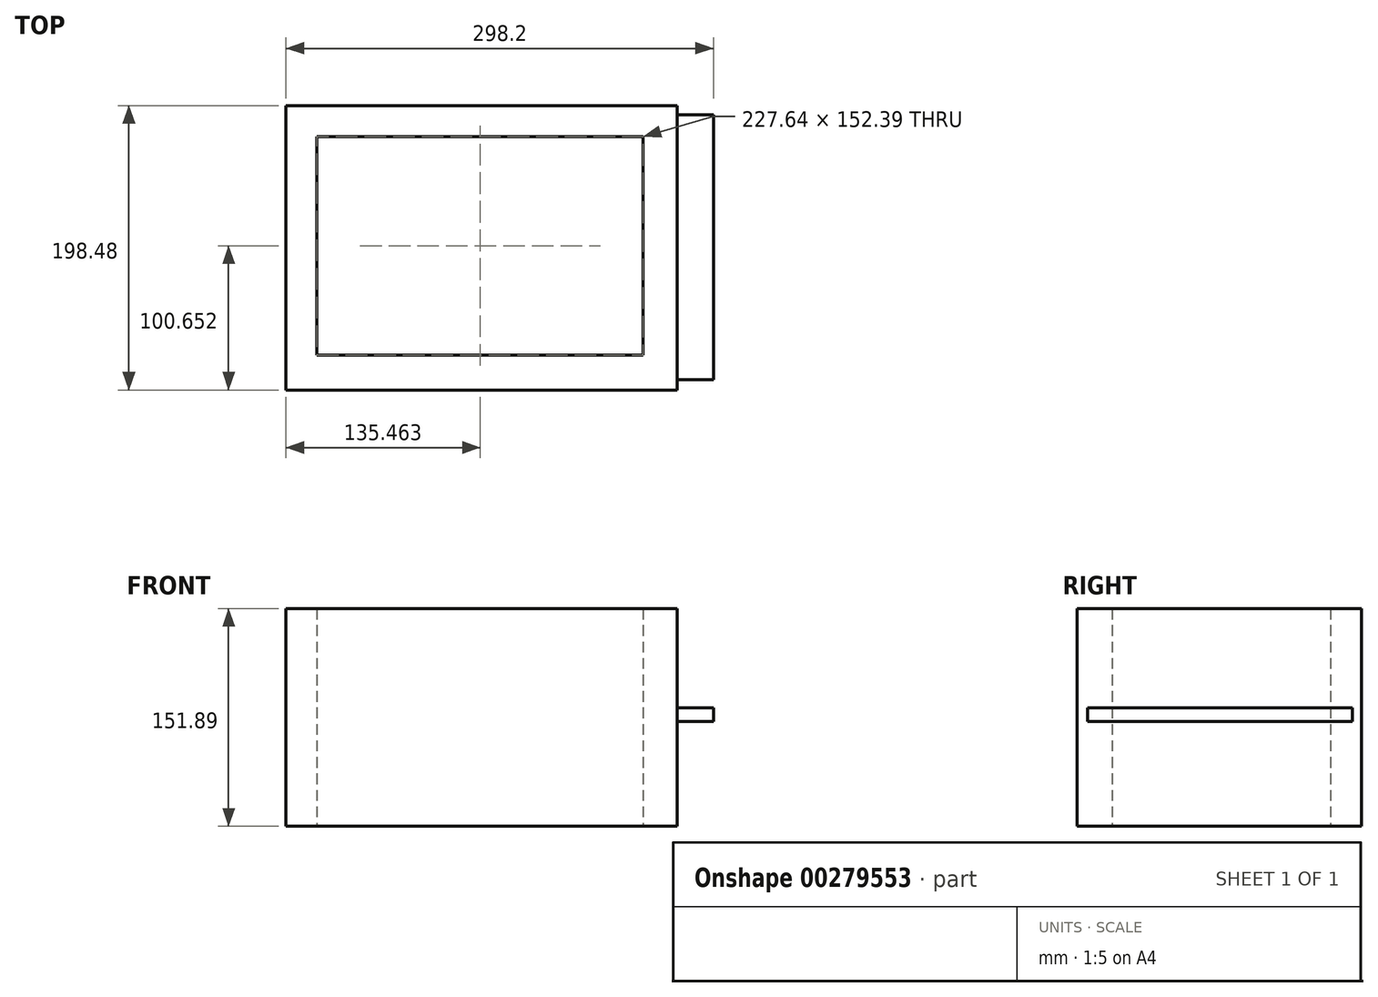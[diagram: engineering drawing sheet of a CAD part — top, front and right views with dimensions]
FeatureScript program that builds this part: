
annotation { "Feature Type Name" : "Feature", "Feature Type Description" : "" }
export const myFeature = defineFeature(function(context is Context, id is Id, definition is map)
    precondition{}
    {
        {
            var Q0;
            Q0=qCreatedBy(makeId("Top.planeOp"),FACE);
            var sketch = newSketch(context, id + "F0", { "sketchPlane" : qUnion([Q0])});
            skLineSegment(sketch, "E0.bottom", {"start": v(-52.57, 51.47) * mm, "end": v(220.23, 51.47) * mm});
            skLineSegment(sketch, "E0.top", {"start": v(-52.57, -147.01) * mm, "end": v(220.23, -147.01) * mm});
            skLineSegment(sketch, "E0.left", {"start": v(-52.57, 51.47) * mm, "end": v(-52.57, -147.01) * mm});
            skLineSegment(sketch, "E0.right", {"start": v(220.23, 51.47) * mm, "end": v(220.23, -147.01) * mm});
            skLineSegment(sketch, "E1.bottom", {"start": v(196.71, 29.84) * mm, "end": v(-30.93, 29.84) * mm});
            skLineSegment(sketch, "E1.top", {"start": v(196.71, -122.55) * mm, "end": v(-30.93, -122.55) * mm});
            skLineSegment(sketch, "E1.left", {"start": v(196.71, 29.84) * mm, "end": v(196.71, -122.55) * mm});
            skLineSegment(sketch, "E1.right", {"start": v(-30.93, 29.84) * mm, "end": v(-30.93, -122.55) * mm});
            skSolve(sketch);
        }
        {
            var Q0;
            Q0=makeQuery(id+"F0.imprint","IMPRINT",FACE,{"disambiguationData":[TD([[makeQuery(id+"F0.imprint","IMPRINT",EDGE,{"derivedFrom":sQuery(id+"F0.wireOp",EDGE,"E0.bottom")}),-1.0]])]});
            extrude(context, id + "F1", {"entities" : qUnion([Q0]), "depth" : 151.9 * mm});
        }
        {
            var Q0;
            Q0=makeQuery(id+"F1.opExtrude","SWEPT_FACE",FACE,{"disambiguationData":[OSD([sQuery(id+"F0.wireOp",EDGE,"E0.right")])]});
            var sketch = newSketch(context, id + "F2", { "sketchPlane" : qUnion([Q0])});
            skLineSegment(sketch, "E2.bottom", {"start": v(-139.82, 82.57) * mm, "end": v(44.94, 82.57) * mm});
            skLineSegment(sketch, "E2.top", {"start": v(-139.82, 73.3) * mm, "end": v(44.94, 73.3) * mm});
            skLineSegment(sketch, "E2.left", {"start": v(-139.82, 82.57) * mm, "end": v(-139.82, 73.3) * mm});
            skLineSegment(sketch, "E2.right", {"start": v(44.94, 82.57) * mm, "end": v(44.94, 73.3) * mm});
            skSolve(sketch);
        }
        {
            var Q0;
            Q0=makeQuery(id+"F2.imprint","IMPRINT",FACE,{"disambiguationData":[TD([[makeQuery(id+"F2.imprint","IMPRINT",EDGE,{"derivedFrom":sQuery(id+"F2.wireOp",EDGE,"E2.bottom")}),-1.0]])]});
            extrude(context, id + "F3", {"entities" : qUnion([Q0]), "operationType" : NewBodyOperationType.ADD, "depth" : 25.4 * mm});
        }
    });
